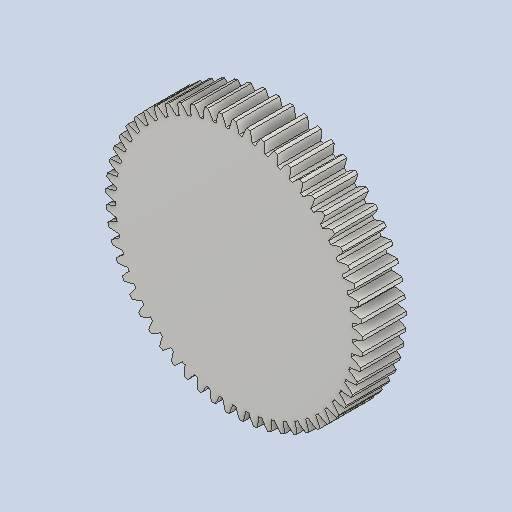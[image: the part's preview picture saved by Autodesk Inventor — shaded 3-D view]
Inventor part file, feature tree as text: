
AUTODESK INVENTOR PART (.ipt)
format: ipt  version: 2023 (Build 270158030, 158C)  size: 372,736 bytes
history: native  units: mm (DEFAULTED — no unit token found)
features: plane x3, other x3, sketch x2, extrude x1
ambient origin geometry x8: Origin, YZ Plane, XZ Plane, XY Plane, X Axis, Y Axis, Z Axis, Center Point
bodies: Solid1 (feature_tree)
feature tree (9):
  extrude  "Extrusion1"  Depth=20.0mm TaperAngle=0.0deg
  plane  "Work Plane2"
  plane  "Work Plane8"
  plane  "Work Plane9"
  other  "Spur Gear"
  sketch  "Sketch1"  dims[d0=118.0mm d1=20.0mm d2=0.0mm]
  sketch  "Sketch2"  dims[d3=114.0mm d4=10.0mm d5=0.0mm d16=80.0mm d17=0.0mm d34=0.551157mm d39=0.0mm d41=0.0mm d43=80.0mm d46=80.0mm d47=0.0mm d48=0.0mm]
  other  "Srf1"
  other  "Pitch Diameter"
